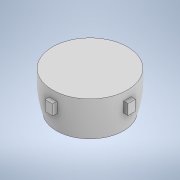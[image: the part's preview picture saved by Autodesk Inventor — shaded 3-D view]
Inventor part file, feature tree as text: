
AUTODESK INVENTOR PART (.ipt)
format: ipt  version: 2021 (Build 250183000, 183)  size: 158,720 bytes
history: native  units: mm
features: sketch x3, extrude x2, other x1
ambient origin geometry x8: Origin, YZ Plane, XZ Plane, XY Plane, X Axis, Y Axis, Z Axis, Center Point
bodies: Solide2 (feature_tree)
feature tree (6):
  other  "Révolution1"
  extrude  "Extrusion1"  TaperAngle=90.0deg  [1 undecoded]
  extrude  "Extrusion2"  Depth=7.0mm
  sketch  "Esquisse1"
  sketch  "Esquisse2"
  sketch  "Esquisse3"
note: 1 required parameter value undecoded (feature->parameter linkage not recoverable at this tier; creation-order binding heuristic only, values carry confidence <= 0.55)
